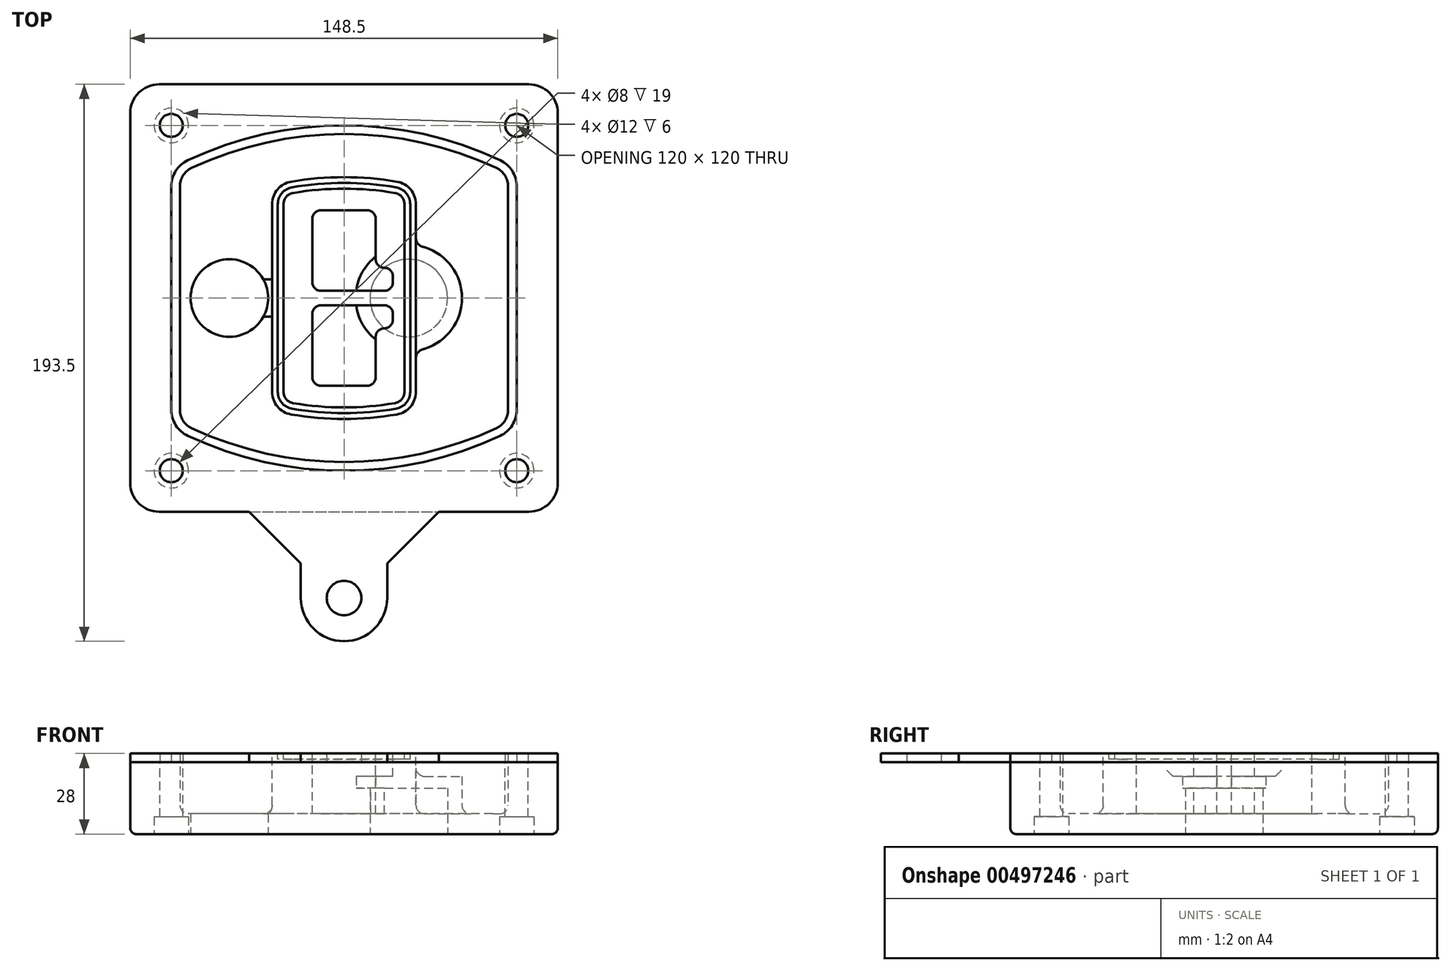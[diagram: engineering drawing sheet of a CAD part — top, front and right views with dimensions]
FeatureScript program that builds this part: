
annotation { "Feature Type Name" : "Feature", "Feature Type Description" : "" }
export const myFeature = defineFeature(function(context is Context, id is Id, definition is map)
    precondition{}
    {
        {
            var Q0;
            Q0=qCreatedBy(makeId("Top.planeOp"),FACE);
            var sketch = newSketch(context, id + "F0", { "sketchPlane" : qUnion([Q0])});
            skPoint(sketch, "E0.rect.middle", {"position": v(0, 0) * mm});
            skLineSegment(sketch, "E1.bottom", {"start": v(-64.25, -74.25) * mm, "end": v(64.25, -74.25) * mm});
            skLineSegment(sketch, "E1.top", {"start": v(-64.25, 74.25) * mm, "end": v(64.25, 74.25) * mm});
            skLineSegment(sketch, "E1.left", {"start": v(-74.25, -64.25) * mm, "end": v(-74.25, 64.25) * mm});
            skLineSegment(sketch, "E1.right", {"start": v(74.25, -64.25) * mm, "end": v(74.25, 64.25) * mm});
            skLineSegment(sketch, "E2", {"start": v(-74.25, 74.25) * mm, "end": v(74.25, -74.25) * mm, "construction": true});
            skLineSegment(sketch, "E3", {"start": v(74.25, 74.25) * mm, "end": v(-74.25, -74.25) * mm, "construction": true});
            skCircle(sketch, "E4", {"center": v(-60, 60) * mm, "radius": 4 * mm});
            skCircle(sketch, "E5", {"center": v(60, 60) * mm, "radius": 4 * mm});
            skCircle(sketch, "E6", {"center": v(60, -60) * mm, "radius": 4 * mm});
            skCircle(sketch, "E7", {"center": v(-60, -60) * mm, "radius": 4 * mm});
            skLineSegment(sketch, "E8", {"start": v(-60, 60) * mm, "end": v(60, 60) * mm, "construction": true});
            skLineSegment(sketch, "E9", {"start": v(60, 60) * mm, "end": v(60, -60) * mm, "construction": true});
            skLineSegment(sketch, "E10", {"start": v(60, -60) * mm, "end": v(-60, -60) * mm, "construction": true});
            skLineSegment(sketch, "E11", {"start": v(-60, -60) * mm, "end": v(-60, 60) * mm, "construction": true});
            skLineSegment(sketch, "E12", {"start": v(-60, 38.83) * mm, "end": v(-60, -38.83) * mm});
            skLineSegment(sketch, "E13", {"start": v(60, 38.83) * mm, "end": v(60, -38.83) * mm});
            skArc(sketch, "E14", {"start": v(54.26, 47.88) * mm, "mid": v(0, 60) * mm, "end": v(-54.26, 47.88) * mm});
            skArc(sketch, "E15", {"start": v(-54.26, -47.88) * mm, "mid": v(0, -60) * mm, "end": v(54.26, -47.88) * mm});
            skLineSegment(sketch, "E16", {"start": v(-60, 0) * mm, "end": v(60, 0) * mm, "construction": true});
            skPoint(sketch, "E17.visualSharp", {"position": v(-60, -45) * mm});
            skArc(sketch, "E17.filletArc", {"start": v(-60, -38.83) * mm, "mid": v(-58.44, -44.2) * mm, "end": v(-54.26, -47.88) * mm});
            skPoint(sketch, "E18.visualSharp", {"position": v(-60, 45) * mm});
            skArc(sketch, "E18.filletArc", {"start": v(-54.26, 47.88) * mm, "mid": v(-58.44, 44.2) * mm, "end": v(-60, 38.83) * mm});
            skPoint(sketch, "E19.visualSharp", {"position": v(60, 45) * mm});
            skArc(sketch, "E19.filletArc", {"start": v(60, 38.83) * mm, "mid": v(58.44, 44.2) * mm, "end": v(54.26, 47.88) * mm});
            skPoint(sketch, "E20.visualSharp", {"position": v(60, -45) * mm});
            skArc(sketch, "E20.filletArc", {"start": v(54.26, -47.88) * mm, "mid": v(58.44, -44.2) * mm, "end": v(60, -38.83) * mm});
            skPoint(sketch, "E21.visualSharp", {"position": v(-74.25, 74.25) * mm});
            skArc(sketch, "E21.filletArc", {"start": v(-64.25, 74.25) * mm, "mid": v(-71.32, 71.32) * mm, "end": v(-74.25, 64.25) * mm});
            skPoint(sketch, "E22.visualSharp", {"position": v(74.25, 74.25) * mm});
            skArc(sketch, "E22.filletArc", {"start": v(74.25, 64.25) * mm, "mid": v(71.32, 71.32) * mm, "end": v(64.25, 74.25) * mm});
            skPoint(sketch, "E23.visualSharp", {"position": v(74.25, -74.25) * mm});
            skArc(sketch, "E23.filletArc", {"start": v(64.25, -74.25) * mm, "mid": v(71.32, -71.32) * mm, "end": v(74.25, -64.25) * mm});
            skPoint(sketch, "E24.visualSharp", {"position": v(-74.25, -74.25) * mm});
            skArc(sketch, "E24.filletArc", {"start": v(-74.25, -64.25) * mm, "mid": v(-71.32, -71.32) * mm, "end": v(-64.25, -74.25) * mm});
            skArc(sketch, "E25.0", {"start": v(57, 38.83) * mm, "mid": v(55.9, 42.58) * mm, "end": v(52.98, 45.17) * mm});
            skLineSegment(sketch, "E25.1", {"start": v(57, 38.83) * mm, "end": v(57, -38.83) * mm});
            skArc(sketch, "E25.2", {"start": v(52.98, -45.17) * mm, "mid": v(55.9, -42.58) * mm, "end": v(57, -38.83) * mm});
            skArc(sketch, "E25.3", {"start": v(-52.98, -45.17) * mm, "mid": v(0, -57) * mm, "end": v(52.98, -45.17) * mm});
            skArc(sketch, "E25.4", {"start": v(-57, -38.83) * mm, "mid": v(-55.9, -42.58) * mm, "end": v(-52.98, -45.17) * mm});
            skArc(sketch, "E25.5", {"start": v(52.98, 45.17) * mm, "mid": v(0, 57) * mm, "end": v(-52.98, 45.17) * mm});
            skLineSegment(sketch, "E25.6", {"start": v(-57, 38.83) * mm, "end": v(-57, -38.83) * mm});
            skArc(sketch, "E25.7", {"start": v(-52.98, 45.17) * mm, "mid": v(-55.9, 42.58) * mm, "end": v(-57, 38.83) * mm});
            skArc(sketch, "E26.0", {"start": v(-55.96, 51.5) * mm, "mid": v(-61.82, 46.33) * mm, "end": v(-64, 38.83) * mm});
            skArc(sketch, "E26.1", {"start": v(55.96, 51.5) * mm, "mid": v(0, 64) * mm, "end": v(-55.96, 51.5) * mm});
            skArc(sketch, "E26.2", {"start": v(64, 38.83) * mm, "mid": v(61.82, 46.33) * mm, "end": v(55.96, 51.5) * mm});
            skLineSegment(sketch, "E26.3", {"start": v(64, 38.83) * mm, "end": v(64, -38.83) * mm});
            skArc(sketch, "E26.4", {"start": v(55.96, -51.5) * mm, "mid": v(61.82, -46.33) * mm, "end": v(64, -38.83) * mm});
            skLineSegment(sketch, "E26.5", {"start": v(-64, 38.83) * mm, "end": v(-64, -38.83) * mm});
            skArc(sketch, "E26.6", {"start": v(-55.96, -51.5) * mm, "mid": v(0, -64) * mm, "end": v(55.96, -51.5) * mm});
            skArc(sketch, "E26.7", {"start": v(-64, -38.83) * mm, "mid": v(-61.82, -46.33) * mm, "end": v(-55.96, -51.5) * mm});
            skSolve(sketch);
        }
        {
            var Q0;
            Q0=makeQuery(id+"F0.imprint","IMPRINT",FACE,{"disambiguationData":[TD([[makeQuery(id+"F0.imprint","IMPRINT",EDGE,{"derivedFrom":sQuery(id+"F0.wireOp",EDGE,"E1.bottom")}),1.0]])]});
            var Q1;
            Q1=makeQuery(id+"F0.imprint","IMPRINT",FACE,{"disambiguationData":[TD([[makeQuery(id+"F0.imprint","IMPRINT",EDGE,{"derivedFrom":sQuery(id+"F0.wireOp",EDGE,"E12")}),1.0]])]});
            var Q2;
            Q2=makeQuery(id+"F0.imprint","IMPRINT",FACE,{"disambiguationData":[TD([[makeQuery(id+"F0.imprint","IMPRINT",EDGE,{"derivedFrom":sQuery(id+"F0.wireOp",EDGE,"E25.0")}),1.0]])]});
            var Q3;
            Q3=makeQuery(id+"F0.imprint","IMPRINT",FACE,{"disambiguationData":[TD([[makeQuery(id+"F0.imprint","IMPRINT",EDGE,{"derivedFrom":sQuery(id+"F0.wireOp",EDGE,"E12")}),-1.0]])]});
            extrude(context, id + "F1", {"entities" : qUnion([Q0, Q1, Q2, Q3]), "oppositeDirection" : true, "depth" : 25 * mm});
        }
        {
            var Q0;
            Q0=makeQuery(id+"F0.imprint","IMPRINT",FACE,{"disambiguationData":[TD([[makeQuery(id+"F0.imprint","IMPRINT",EDGE,{"derivedFrom":sQuery(id+"F0.wireOp",EDGE,"E12")}),1.0]])]});
            extrude(context, id + "F2", {"entities" : qUnion([Q0]), "operationType" : NewBodyOperationType.ADD, "depth" : 3 * mm});
        }
        {
            var Q0;
            Q0=makeQuery(id+"F0.imprint","IMPRINT",FACE,{"disambiguationData":[TD([[makeQuery(id+"F0.imprint","IMPRINT",EDGE,{"derivedFrom":sQuery(id+"F0.wireOp",EDGE,"E25.0")}),1.0]])]});
            extrude(context, id + "F3", {"entities" : qUnion([Q0]), "operationType" : NewBodyOperationType.REMOVE, "oppositeDirection" : true, "depth" : 18 * mm});
        }
        {
            var Q0;
            Q0=makeQuery(id+"F2.opExtrude","CAP_FACE",FACE,{"disambiguationData":[OSD([sQuery(id+"F0.wireOp",EDGE,"E12"),sQuery(id+"F0.wireOp",EDGE,"E13"),sQuery(id+"F0.wireOp",EDGE,"E14"),sQuery(id+"F0.wireOp",EDGE,"E15"),sQuery(id+"F0.wireOp",EDGE,"E17.filletArc"),sQuery(id+"F0.wireOp",EDGE,"E18.filletArc"),sQuery(id+"F0.wireOp",EDGE,"E19.filletArc"),sQuery(id+"F0.wireOp",EDGE,"E20.filletArc"),sQuery(id+"F0.wireOp",EDGE,"E25.0"),sQuery(id+"F0.wireOp",EDGE,"E25.1"),sQuery(id+"F0.wireOp",EDGE,"E25.2"),sQuery(id+"F0.wireOp",EDGE,"E25.3"),sQuery(id+"F0.wireOp",EDGE,"E25.4"),sQuery(id+"F0.wireOp",EDGE,"E25.5"),sQuery(id+"F0.wireOp",EDGE,"E25.6"),sQuery(id+"F0.wireOp",EDGE,"E25.7")])],"isStart":false});
            var sketch = newSketch(context, id + "F4", { "sketchPlane" : qUnion([Q0])});
            skArc(sketch, "E27.0", {"start": v(-18.34, -40.45) * mm, "mid": v(0, -42) * mm, "end": v(18.34, -40.45) * mm});
            skArc(sketch, "E28.0", {"start": v(18.34, 40.45) * mm, "mid": v(0, 42) * mm, "end": v(-18.34, 40.45) * mm});
            skLineSegment(sketch, "E29", {"start": v(-25, 32.57) * mm, "end": v(-25, -32.57) * mm});
            skLineSegment(sketch, "E30", {"start": v(25, 32.57) * mm, "end": v(25, -32.57) * mm});
            skLineSegment(sketch, "E31", {"start": v(-25, 39.1) * mm, "end": v(25, 39.1) * mm, "construction": true});
            skLineSegment(sketch, "E32", {"start": v(-25, -39.1) * mm, "end": v(25, -39.1) * mm, "construction": true});
            skPoint(sketch, "E33.visualSharp", {"position": v(-25, 39.1) * mm});
            skArc(sketch, "E33.filletArc", {"start": v(-18.34, 40.45) * mm, "mid": v(-23.11, 37.73) * mm, "end": v(-25, 32.57) * mm});
            skPoint(sketch, "E34.visualSharp", {"position": v(25, 39.1) * mm});
            skArc(sketch, "E34.filletArc", {"start": v(25, 32.57) * mm, "mid": v(23.11, 37.73) * mm, "end": v(18.34, 40.45) * mm});
            skPoint(sketch, "E35.visualSharp", {"position": v(25, -39.1) * mm});
            skArc(sketch, "E35.filletArc", {"start": v(18.34, -40.45) * mm, "mid": v(23.11, -37.73) * mm, "end": v(25, -32.57) * mm});
            skPoint(sketch, "E36.visualSharp", {"position": v(-25, -39.1) * mm});
            skArc(sketch, "E36.filletArc", {"start": v(-25, -32.57) * mm, "mid": v(-23.11, -37.73) * mm, "end": v(-18.34, -40.45) * mm});
            skArc(sketch, "E37.0", {"start": v(52.98, 45.17) * mm, "mid": v(0, 57) * mm, "end": v(-52.98, 45.17) * mm});
            skArc(sketch, "E37.1", {"start": v(-52.98, 45.17) * mm, "mid": v(-55.9, 42.58) * mm, "end": v(-57, 38.83) * mm});
            skLineSegment(sketch, "E37.2", {"start": v(-57, 38.83) * mm, "end": v(-57, -38.83) * mm});
            skArc(sketch, "E37.3", {"start": v(-57, -38.83) * mm, "mid": v(-55.9, -42.58) * mm, "end": v(-52.98, -45.17) * mm});
            skArc(sketch, "E37.4", {"start": v(-52.98, -45.17) * mm, "mid": v(0, -57) * mm, "end": v(52.98, -45.17) * mm});
            skArc(sketch, "E37.5", {"start": v(52.98, -45.17) * mm, "mid": v(55.9, -42.58) * mm, "end": v(57, -38.83) * mm});
            skLineSegment(sketch, "E37.6", {"start": v(57, 38.83) * mm, "end": v(57, -38.83) * mm});
            skArc(sketch, "E37.7", {"start": v(57, 38.83) * mm, "mid": v(55.9, 42.58) * mm, "end": v(52.98, 45.17) * mm});
            skLineSegment(sketch, "E38.0", {"start": v(23, 32.57) * mm, "end": v(23, -32.57) * mm});
            skArc(sketch, "E38.1", {"start": v(18, -38.48) * mm, "mid": v(21.58, -36.44) * mm, "end": v(23, -32.57) * mm});
            skArc(sketch, "E38.2", {"start": v(-18, -38.48) * mm, "mid": v(0, -40) * mm, "end": v(18, -38.48) * mm});
            skArc(sketch, "E38.3", {"start": v(-23, -32.57) * mm, "mid": v(-21.58, -36.44) * mm, "end": v(-18, -38.48) * mm});
            skLineSegment(sketch, "E38.4", {"start": v(-23, 32.57) * mm, "end": v(-23, -32.57) * mm});
            skArc(sketch, "E38.5", {"start": v(23, 32.57) * mm, "mid": v(21.58, 36.44) * mm, "end": v(18, 38.48) * mm});
            skArc(sketch, "E38.6", {"start": v(-18, 38.48) * mm, "mid": v(-21.58, 36.44) * mm, "end": v(-23, 32.57) * mm});
            skArc(sketch, "E38.7", {"start": v(18, 38.48) * mm, "mid": v(0, 40) * mm, "end": v(-18, 38.48) * mm});
            skArc(sketch, "E39.0", {"start": v(21, 32.57) * mm, "mid": v(20.06, 35.15) * mm, "end": v(17.67, 36.5) * mm});
            skLineSegment(sketch, "E39.1", {"start": v(21, 32.57) * mm, "end": v(21, -32.57) * mm});
            skArc(sketch, "E39.2", {"start": v(17.67, -36.5) * mm, "mid": v(20.06, -35.15) * mm, "end": v(21, -32.57) * mm});
            skArc(sketch, "E39.3", {"start": v(-17.67, -36.5) * mm, "mid": v(0, -38) * mm, "end": v(17.67, -36.5) * mm});
            skArc(sketch, "E39.4", {"start": v(-21, -32.57) * mm, "mid": v(-20.06, -35.15) * mm, "end": v(-17.67, -36.5) * mm});
            skArc(sketch, "E39.5", {"start": v(17.67, 36.5) * mm, "mid": v(0, 38) * mm, "end": v(-17.67, 36.5) * mm});
            skLineSegment(sketch, "E39.6", {"start": v(-21, 32.57) * mm, "end": v(-21, -32.57) * mm});
            skArc(sketch, "E39.7", {"start": v(-17.67, 36.5) * mm, "mid": v(-20.06, 35.15) * mm, "end": v(-21, 32.57) * mm});
            skLineSegment(sketch, "E40", {"start": v(-25, 0) * mm, "end": v(25, 0) * mm, "construction": true});
            skLineSegment(sketch, "E41", {"start": v(-11, 5.5) * mm, "end": v(-11, 27.5) * mm});
            skLineSegment(sketch, "E42", {"start": v(-8, 30.5) * mm, "end": v(8, 30.5) * mm});
            skLineSegment(sketch, "E43", {"start": v(11, 27.5) * mm, "end": v(11, 13.5) * mm});
            skLineSegment(sketch, "E44", {"start": v(14, 10.5) * mm, "end": v(14, 10.5) * mm});
            skLineSegment(sketch, "E45", {"start": v(17, 7.5) * mm, "end": v(17, 5.5) * mm});
            skLineSegment(sketch, "E46", {"start": v(14, 2.5) * mm, "end": v(-8, 2.5) * mm});
            skPoint(sketch, "E47.visualSharp", {"position": v(-11, 30.5) * mm});
            skArc(sketch, "E47.filletArc", {"start": v(-8, 30.5) * mm, "mid": v(-10.12, 29.62) * mm, "end": v(-11, 27.5) * mm});
            skPoint(sketch, "E48.visualSharp", {"position": v(11, 30.5) * mm});
            skArc(sketch, "E48.filletArc", {"start": v(11, 27.5) * mm, "mid": v(10.12, 29.62) * mm, "end": v(8, 30.5) * mm});
            skPoint(sketch, "E49.visualSharp", {"position": v(11, 10.5) * mm});
            skArc(sketch, "E49.filletArc", {"start": v(11, 13.5) * mm, "mid": v(11.88, 11.38) * mm, "end": v(14, 10.5) * mm});
            skPoint(sketch, "E50.visualSharp", {"position": v(17, 10.5) * mm});
            skArc(sketch, "E50.filletArc", {"start": v(17, 7.5) * mm, "mid": v(16.12, 9.62) * mm, "end": v(14, 10.5) * mm});
            skPoint(sketch, "E51.visualSharp", {"position": v(17, 2.5) * mm});
            skArc(sketch, "E51.filletArc", {"start": v(14, 2.5) * mm, "mid": v(16.12, 3.38) * mm, "end": v(17, 5.5) * mm});
            skPoint(sketch, "E52.visualSharp", {"position": v(-11, 2.5) * mm});
            skArc(sketch, "E52.filletArc", {"start": v(-11, 5.5) * mm, "mid": v(-10.12, 3.38) * mm, "end": v(-8, 2.5) * mm});
            skLineSegment(sketch, "E53.0.MirrorCS", {"start": v(14, -2.5) * mm, "end": v(-8, -2.5) * mm});
            skArc(sketch, "E54.0.MirrorCS", {"start": v(-11, -5.5) * mm, "mid": v(-10.12, -3.38) * mm, "end": v(-8, -2.5) * mm});
            skLineSegment(sketch, "E55.0.MirrorCS", {"start": v(-11, -5.5) * mm, "end": v(-11, -27.5) * mm});
            skArc(sketch, "E56.0.MirrorCS", {"start": v(-8, -30.5) * mm, "mid": v(-10.12, -29.62) * mm, "end": v(-11, -27.5) * mm});
            skLineSegment(sketch, "E57.0.MirrorCS", {"start": v(-8, -30.5) * mm, "end": v(8, -30.5) * mm});
            skArc(sketch, "E58.0.MirrorCS", {"start": v(11, -27.5) * mm, "mid": v(10.12, -29.62) * mm, "end": v(8, -30.5) * mm});
            skLineSegment(sketch, "E59.0.MirrorCS", {"start": v(11, -27.5) * mm, "end": v(11, -13.5) * mm});
            skArc(sketch, "E60.0.MirrorCS", {"start": v(11, -13.5) * mm, "mid": v(11.88, -11.38) * mm, "end": v(14, -10.5) * mm});
            skArc(sketch, "E61.0.MirrorCS", {"start": v(17, -7.5) * mm, "mid": v(16.12, -9.62) * mm, "end": v(14, -10.5) * mm});
            skLineSegment(sketch, "E62.0.MirrorCS", {"start": v(17, -7.5) * mm, "end": v(17, -5.5) * mm});
            skArc(sketch, "E63.0.MirrorCS", {"start": v(14, -2.5) * mm, "mid": v(16.12, -3.38) * mm, "end": v(17, -5.5) * mm});
            skSolve(sketch);
        }
        {
            var Q0;
            Q0=makeQuery(id+"F4.imprint","IMPRINT",FACE,{"disambiguationData":[TD([[makeQuery(id+"F4.imprint","IMPRINT",EDGE,{"derivedFrom":sQuery(id+"F4.wireOp",EDGE,"E27.0")}),1.0]])]});
            var Q1;
            Q1=makeQuery(id+"F4.imprint","IMPRINT",FACE,{"disambiguationData":[TD([[makeQuery(id+"F4.imprint","IMPRINT",EDGE,{"derivedFrom":sQuery(id+"F4.wireOp",EDGE,"E38.0")}),-1.0]])]});
            var Q2;
            Q2=makeQuery(id+"F4.imprint","IMPRINT",FACE,{"disambiguationData":[TD([[makeQuery(id+"F4.imprint","IMPRINT",EDGE,{"derivedFrom":sQuery(id+"F4.wireOp",EDGE,"E39.0")}),1.0]])]});
            extrude(context, id + "F5", {"entities" : qUnion([Q0, Q1, Q2]), "operationType" : NewBodyOperationType.ADD, "endBound" : BoundingType.UP_TO_NEXT, "oppositeDirection" : true, "depth" : 25 * mm});
        }
        {
            var Q0;
            Q0=makeQuery(id+"F4.imprint","IMPRINT",FACE,{"disambiguationData":[TD([[makeQuery(id+"F4.imprint","IMPRINT",EDGE,{"derivedFrom":sQuery(id+"F4.wireOp",EDGE,"E38.0")}),-1.0]])]});
            extrude(context, id + "F6", {"entities" : qUnion([Q0]), "operationType" : NewBodyOperationType.REMOVE, "oppositeDirection" : true, "depth" : 2 * mm});
        }
        {
            var Q0;
            Q0=makeQuery(id+"F1.opExtrude","CAP_FACE",FACE,{"disambiguationData":[OSD([sQuery(id+"F0.wireOp",EDGE,"E1.bottom"),sQuery(id+"F0.wireOp",EDGE,"E1.top"),sQuery(id+"F0.wireOp",EDGE,"E1.left"),sQuery(id+"F0.wireOp",EDGE,"E1.right"),sQuery(id+"F0.wireOp",EDGE,"E4"),sQuery(id+"F0.wireOp",EDGE,"E5"),sQuery(id+"F0.wireOp",EDGE,"E6"),sQuery(id+"F0.wireOp",EDGE,"E7"),sQuery(id+"F0.wireOp",EDGE,"E21.filletArc"),sQuery(id+"F0.wireOp",EDGE,"E22.filletArc"),sQuery(id+"F0.wireOp",EDGE,"E23.filletArc"),sQuery(id+"F0.wireOp",EDGE,"E24.filletArc")])],"isStart":false});
            var sketch = newSketch(context, id + "F7", { "sketchPlane" : qUnion([Q0])});
            skCircle(sketch, "E64", {"center": v(22.5, 0) * mm, "radius": 13.47 * mm});
            skCircle(sketch, "E65", {"center": v(-39.81, 0) * mm, "radius": 13.47 * mm});
            skLineSegment(sketch, "E66", {"start": v(74.25, 0) * mm, "end": v(-74.25, 0) * mm});
            skCircle(sketch, "E67", {"center": v(22.5, 0) * mm, "radius": 18.47 * mm});
            skCircle(sketch, "E68", {"center": v(60, -60) * mm, "radius": 6 * mm});
            skCircle(sketch, "E69", {"center": v(-60, -60) * mm, "radius": 6 * mm});
            skCircle(sketch, "E70", {"center": v(-60, 60) * mm, "radius": 6 * mm});
            skCircle(sketch, "E71", {"center": v(60, 60) * mm, "radius": 6 * mm});
            skSolve(sketch);
        }
        {
            var Q0;
            {var subQ1=sQuery(id+"F7.wireOp",EDGE,"E66");var subQ4=sQuery(id+"F7.wireOp",EDGE,"E64");var subQ6=makeQuery(id+"F7.imprint","INTERSECT",VERTEX,{"disambiguationData":[OD(0.0)],"derivedFrom":[subQ4,subQ1]});Q0=makeQuery(id+"F7.imprint","IMPRINT",FACE,{"disambiguationData":[TD([[makeQuery(id+"F7.imprint","IMPRINT",EDGE,{"disambiguationData":[TD([[subQ6,-1.0]])],"derivedFrom":subQ4}),-1.0]])]});}
            var Q1;
            {var subQ0=sQuery(id+"F7.wireOp",EDGE,"E66");var subQ1=sQuery(id+"F7.wireOp",EDGE,"E64");var subQ3=makeQuery(id+"F7.imprint","INTERSECT",VERTEX,{"disambiguationData":[OD(0.0)],"derivedFrom":[subQ1,subQ0]});Q1=makeQuery(id+"F7.imprint","IMPRINT",FACE,{"disambiguationData":[TD([[makeQuery(id+"F7.imprint","IMPRINT",EDGE,{"disambiguationData":[TD([[subQ3,-1.0]])],"derivedFrom":subQ1}),1.0]])]});}
            var Q2;
            {var subQ0=sQuery(id+"F7.wireOp",EDGE,"E66");var subQ1=sQuery(id+"F7.wireOp",EDGE,"E64");var subQ3=makeQuery(id+"F7.imprint","INTERSECT",VERTEX,{"disambiguationData":[OD(0.0)],"derivedFrom":[subQ1,subQ0]});Q2=makeQuery(id+"F7.imprint","IMPRINT",FACE,{"disambiguationData":[TD([[makeQuery(id+"F7.imprint","IMPRINT",EDGE,{"disambiguationData":[TD([[subQ3,1.0]])],"derivedFrom":subQ1}),1.0]])]});}
            var Q3;
            {var subQ1=sQuery(id+"F7.wireOp",EDGE,"E66");var subQ4=sQuery(id+"F7.wireOp",EDGE,"E64");var subQ6=makeQuery(id+"F7.imprint","INTERSECT",VERTEX,{"disambiguationData":[OD(0.0)],"derivedFrom":[subQ4,subQ1]});Q3=makeQuery(id+"F7.imprint","IMPRINT",FACE,{"disambiguationData":[TD([[makeQuery(id+"F7.imprint","IMPRINT",EDGE,{"disambiguationData":[TD([[subQ6,1.0]])],"derivedFrom":subQ4}),-1.0]])]});}
            extrude(context, id + "F8", {"entities" : qUnion([Q0, Q1, Q2, Q3]), "operationType" : NewBodyOperationType.ADD, "oppositeDirection" : true, "depth" : 20 * mm});
        }
        {
            var Q0;
            {var subQ0=sQuery(id+"F7.wireOp",EDGE,"E66");var subQ1=sQuery(id+"F7.wireOp",EDGE,"E64");var subQ3=makeQuery(id+"F7.imprint","INTERSECT",VERTEX,{"disambiguationData":[OD(0.0)],"derivedFrom":[subQ1,subQ0]});Q0=makeQuery(id+"F7.imprint","IMPRINT",FACE,{"disambiguationData":[TD([[makeQuery(id+"F7.imprint","IMPRINT",EDGE,{"disambiguationData":[TD([[subQ3,-1.0]])],"derivedFrom":subQ1}),1.0]])]});}
            var Q1;
            {var subQ0=sQuery(id+"F7.wireOp",EDGE,"E66");var subQ1=sQuery(id+"F7.wireOp",EDGE,"E64");var subQ3=makeQuery(id+"F7.imprint","INTERSECT",VERTEX,{"disambiguationData":[OD(0.0)],"derivedFrom":[subQ1,subQ0]});Q1=makeQuery(id+"F7.imprint","IMPRINT",FACE,{"disambiguationData":[TD([[makeQuery(id+"F7.imprint","IMPRINT",EDGE,{"disambiguationData":[TD([[subQ3,1.0]])],"derivedFrom":subQ1}),1.0]])]});}
            extrude(context, id + "F9", {"entities" : qUnion([Q0, Q1]), "operationType" : NewBodyOperationType.REMOVE, "oppositeDirection" : true, "depth" : 16 * mm});
        }
        {
            var Q0;
            {var subQ0=sQuery(id+"F7.wireOp",EDGE,"E66");var subQ1=sQuery(id+"F7.wireOp",EDGE,"E65");var subQ3=makeQuery(id+"F7.imprint","INTERSECT",VERTEX,{"disambiguationData":[OD(0.0)],"derivedFrom":[subQ1,subQ0]});Q0=makeQuery(id+"F7.imprint","IMPRINT",FACE,{"disambiguationData":[TD([[makeQuery(id+"F7.imprint","IMPRINT",EDGE,{"disambiguationData":[TD([[subQ3,-1.0]])],"derivedFrom":subQ1}),1.0]])]});}
            var Q1;
            {var subQ0=sQuery(id+"F7.wireOp",EDGE,"E66");var subQ1=sQuery(id+"F7.wireOp",EDGE,"E65");var subQ3=makeQuery(id+"F7.imprint","INTERSECT",VERTEX,{"disambiguationData":[OD(0.0)],"derivedFrom":[subQ1,subQ0]});Q1=makeQuery(id+"F7.imprint","IMPRINT",FACE,{"disambiguationData":[TD([[makeQuery(id+"F7.imprint","IMPRINT",EDGE,{"disambiguationData":[TD([[subQ3,1.0]])],"derivedFrom":subQ1}),1.0]])]});}
            extrude(context, id + "F10", {"entities" : qUnion([Q0, Q1]), "operationType" : NewBodyOperationType.REMOVE, "oppositeDirection" : true, "depth" : 25 * mm});
        }
        {
            var Q0;
            Q0=makeQuery(id+"F7.imprint","IMPRINT",FACE,{"disambiguationData":[TD([[makeQuery(id+"F7.imprint","IMPRINT",EDGE,{"derivedFrom":sQuery(id+"F7.wireOp",EDGE,"E68")}),1.0]])]});
            var Q1;
            Q1=makeQuery(id+"F7.imprint","IMPRINT",FACE,{"disambiguationData":[TD([[makeQuery(id+"F7.imprint","IMPRINT",EDGE,{"derivedFrom":makeQuery(id+"F1.opExtrude","CAP_EDGE",EDGE,{"disambiguationData":[OSD([sQuery(id+"F0.wireOp",EDGE,"E5")])],"isStart":false})}),-1.0]])]});
            var Q2;
            Q2=makeQuery(id+"F7.imprint","IMPRINT",FACE,{"disambiguationData":[TD([[makeQuery(id+"F7.imprint","IMPRINT",EDGE,{"derivedFrom":sQuery(id+"F7.wireOp",EDGE,"E69")}),1.0]])]});
            var Q3;
            Q3=makeQuery(id+"F7.imprint","IMPRINT",FACE,{"disambiguationData":[TD([[makeQuery(id+"F7.imprint","IMPRINT",EDGE,{"derivedFrom":makeQuery(id+"F1.opExtrude","CAP_EDGE",EDGE,{"disambiguationData":[OSD([sQuery(id+"F0.wireOp",EDGE,"E4")])],"isStart":false})}),-1.0]])]});
            var Q4;
            Q4=makeQuery(id+"F7.imprint","IMPRINT",FACE,{"disambiguationData":[TD([[makeQuery(id+"F7.imprint","IMPRINT",EDGE,{"derivedFrom":sQuery(id+"F7.wireOp",EDGE,"E70")}),1.0]])]});
            var Q5;
            Q5=makeQuery(id+"F7.imprint","IMPRINT",FACE,{"disambiguationData":[TD([[makeQuery(id+"F7.imprint","IMPRINT",EDGE,{"derivedFrom":makeQuery(id+"F1.opExtrude","CAP_EDGE",EDGE,{"disambiguationData":[OSD([sQuery(id+"F0.wireOp",EDGE,"E7")])],"isStart":false})}),-1.0]])]});
            var Q6;
            Q6=makeQuery(id+"F7.imprint","IMPRINT",FACE,{"disambiguationData":[TD([[makeQuery(id+"F7.imprint","IMPRINT",EDGE,{"derivedFrom":sQuery(id+"F7.wireOp",EDGE,"E71")}),1.0]])]});
            var Q7;
            Q7=makeQuery(id+"F7.imprint","IMPRINT",FACE,{"disambiguationData":[TD([[makeQuery(id+"F7.imprint","IMPRINT",EDGE,{"derivedFrom":makeQuery(id+"F1.opExtrude","CAP_EDGE",EDGE,{"disambiguationData":[OSD([sQuery(id+"F0.wireOp",EDGE,"E6")])],"isStart":false})}),-1.0]])]});
            extrude(context, id + "F11", {"entities" : qUnion([Q0, Q1, Q2, Q3, Q4, Q5, Q6, Q7]), "operationType" : NewBodyOperationType.REMOVE, "oppositeDirection" : true, "depth" : 6 * mm});
        }
        {
            var Q0;
            Q0=makeQuery(id+"F9.boolean.opBoolean","COPY",FACE,{"derivedFrom":makeQuery(id+"F9.opExtrude","CAP_FACE",FACE,{"disambiguationData":[OSD([sQuery(id+"F7.wireOp",EDGE,"E64")])],"isStart":false})});
            var sketch = newSketch(context, id + "F12", { "sketchPlane" : qUnion([Q0])});
            skArc(sketch, "E72.0", {"start": v(11, 14.45) * mm, "mid": v(6.45, 9.13) * mm, "end": v(4.2, 2.5) * mm});
            skArc(sketch, "E72.1", {"start": v(4.2, -2.5) * mm, "mid": v(6.45, -9.13) * mm, "end": v(11, -14.45) * mm});
            skLineSegment(sketch, "E73", {"start": v(4.2, -2.5) * mm, "end": v(14, -2.5) * mm});
            skLineSegment(sketch, "E74.0", {"start": v(14, 2.5) * mm, "end": v(4.2, 2.5) * mm});
            skArc(sketch, "E74.1", {"start": v(14, 2.5) * mm, "mid": v(16.12, 3.38) * mm, "end": v(17, 5.5) * mm});
            skLineSegment(sketch, "E74.2", {"start": v(17, 7.5) * mm, "end": v(17, 5.5) * mm});
            skArc(sketch, "E74.3", {"start": v(17, 7.5) * mm, "mid": v(16.12, 9.62) * mm, "end": v(14, 10.5) * mm});
            skArc(sketch, "E74.4", {"start": v(11, 13.5) * mm, "mid": v(11.88, 11.38) * mm, "end": v(14, 10.5) * mm});
            skLineSegment(sketch, "E74.5", {"start": v(11, 14.45) * mm, "end": v(11, 13.5) * mm});
            skLineSegment(sketch, "E74.7", {"start": v(14, -2.5) * mm, "end": v(4.2, -2.5) * mm});
            skArc(sketch, "E74.8", {"start": v(14, -2.5) * mm, "mid": v(16.12, -3.38) * mm, "end": v(17, -5.5) * mm});
            skLineSegment(sketch, "E74.9", {"start": v(17, -7.5) * mm, "end": v(17, -5.5) * mm});
            skArc(sketch, "E74.10", {"start": v(17, -7.5) * mm, "mid": v(16.12, -9.62) * mm, "end": v(14, -10.5) * mm});
            skArc(sketch, "E74.11", {"start": v(11, -13.5) * mm, "mid": v(11.88, -11.38) * mm, "end": v(14, -10.5) * mm});
            skLineSegment(sketch, "E74.12", {"start": v(11, -14.45) * mm, "end": v(11, -13.5) * mm});
            skPoint(sketch, "E75.orphan", {"position": v(11, -27.5) * mm});
            skPoint(sketch, "E76.orphan", {"position": v(-8, -2.5) * mm});
            skPoint(sketch, "E77.orphan", {"position": v(-8, 2.5) * mm});
            skPoint(sketch, "E78.orphan", {"position": v(11, 27.5) * mm});
            skSolve(sketch);
        }
        {
            var Q0;
            {var subQ7=sQuery(id+"F12.wireOp",EDGE,"E72.0");var subQ14=sQuery(id+"F12.wireOp",EDGE,"E72.1");var subQ16=sQuery(id+"F12.wireOp",EDGE,"E74.1");var subQ18=sQuery(id+"F12.wireOp",EDGE,"E74.8");Q0=qUnion([makeQuery(id+"F12.imprint","IMPRINT",FACE,{"disambiguationData":[TD([[makeQuery(id+"F12.imprint","IMPRINT",EDGE,{"derivedFrom":subQ7}),1.0]])]}),makeQuery(id+"F12.imprint","IMPRINT",FACE,{"disambiguationData":[TD([[makeQuery(id+"F12.imprint","IMPRINT",EDGE,{"derivedFrom":subQ14}),1.0]])]}),makeQuery(id+"F12.imprint","IMPRINT",FACE,{"disambiguationData":[TD([[makeQuery(id+"F12.imprint","IMPRINT",EDGE,{"derivedFrom":subQ16}),1.0]])]}),makeQuery(id+"F12.imprint","IMPRINT",FACE,{"disambiguationData":[TD([[makeQuery(id+"F12.imprint","IMPRINT",EDGE,{"derivedFrom":subQ18}),-1.0]])]})]);}
            var Q1;
            Q1=makeQuery(id+"F5.boolean.opBoolean","SPLIT",FACE,{"disambiguationData":[TD([makeQuery(id+"F5.opExtrude","SWEPT_FACE",FACE,{"disambiguationData":[OSD([sQuery(id+"F4.wireOp",EDGE,"E41")])]})])],"derivedFrom":makeQuery(id+"F3.boolean.opBoolean","COPY",FACE,{"derivedFrom":makeQuery(id+"F3.opExtrude","CAP_FACE",FACE,{"disambiguationData":[OSD([sQuery(id+"F0.wireOp",EDGE,"E25.0"),sQuery(id+"F0.wireOp",EDGE,"E25.1"),sQuery(id+"F0.wireOp",EDGE,"E25.2"),sQuery(id+"F0.wireOp",EDGE,"E25.3"),sQuery(id+"F0.wireOp",EDGE,"E25.4"),sQuery(id+"F0.wireOp",EDGE,"E25.5"),sQuery(id+"F0.wireOp",EDGE,"E25.6"),sQuery(id+"F0.wireOp",EDGE,"E25.7")])],"isStart":false})})});
            extrude(context, id + "F13", {"entities" : qUnion([Q0]), "operationType" : NewBodyOperationType.REMOVE, "endBound" : BoundingType.UP_TO_SURFACE, "endBoundEntityFace" : qUnion([Q1]), "depth" : 25 * mm});
        }
        {
            var Q0;
            Q0=makeQuery(id+"F3.boolean.opBoolean","COPY",EDGE,{"derivedFrom":makeQuery(id+"F3.opExtrude","CAP_EDGE",EDGE,{"disambiguationData":[OSD([sQuery(id+"F0.wireOp",EDGE,"E25.6")])],"isStart":false})});
            var Q1;
            Q1=makeQuery(id+"F8.boolean.opBoolean","INTERSECT",EDGE,{"derivedFrom":[makeQuery(id+"F5.opExtrude","SWEPT_FACE",FACE,{"disambiguationData":[OSD([sQuery(id+"F4.wireOp",EDGE,"E30")])]}),makeQuery(id+"F8.opExtrude","CAP_FACE",FACE,{"disambiguationData":[OSD([sQuery(id+"F7.wireOp",EDGE,"E67")])],"isStart":false})]});
            var Q2;
            Q2=makeQuery(id+"F8.boolean.opBoolean","INTERSECT",EDGE,{"disambiguationData":[OD(1.0)],"derivedFrom":[makeQuery(id+"F5.opExtrude","SWEPT_FACE",FACE,{"disambiguationData":[OSD([sQuery(id+"F4.wireOp",EDGE,"E30")])]}),makeQuery(id+"F8.opExtrude","SWEPT_FACE",FACE,{"disambiguationData":[OSD([sQuery(id+"F7.wireOp",EDGE,"E67")])]})]});
            var Q3;
            {var subQ0=sQuery(id+"F4.wireOp",EDGE,"E30");Q3=makeQuery(id+"F8.boolean.opBoolean","SPLIT",EDGE,{"disambiguationData":[TD([makeQuery(id+"F5.opExtrude","SWEPT_FACE",FACE,{"disambiguationData":[OSD([sQuery(id+"F4.wireOp",EDGE,"E35.filletArc")])]})])],"derivedFrom":makeQuery(id+"F5.opExtrude","CAP_EDGE",EDGE,{"disambiguationData":[OSD([subQ0])],"isStart":false})});}
            var Q4;
            {var subQ0=sQuery(id+"F0.wireOp",EDGE,"E25.7");var subQ1=sQuery(id+"F0.wireOp",EDGE,"E25.1");var subQ2=sQuery(id+"F0.wireOp",EDGE,"E25.6");var subQ3=sQuery(id+"F0.wireOp",EDGE,"E25.5");var subQ4=sQuery(id+"F0.wireOp",EDGE,"E25.4");var subQ5=sQuery(id+"F0.wireOp",EDGE,"E25.0");var subQ6=sQuery(id+"F0.wireOp",EDGE,"E25.2");var subQ7=sQuery(id+"F0.wireOp",EDGE,"E25.3");Q4=makeQuery(id+"F8.boolean.opBoolean","INTERSECT",EDGE,{"derivedFrom":[makeQuery(id+"F5.boolean.opBoolean","SPLIT",FACE,{"disambiguationData":[TD([makeQuery(id+"F2.opExtrude","SWEPT_FACE",FACE,{"disambiguationData":[OSD([subQ5])]})])],"derivedFrom":makeQuery(id+"F3.boolean.opBoolean","COPY",FACE,{"derivedFrom":makeQuery(id+"F3.opExtrude","CAP_FACE",FACE,{"disambiguationData":[OSD([subQ5,subQ1,subQ6,subQ7,subQ4,subQ3,subQ2,subQ0])],"isStart":false})})}),makeQuery(id+"F8.opExtrude","SWEPT_FACE",FACE,{"disambiguationData":[OSD([sQuery(id+"F7.wireOp",EDGE,"E67")])]})]});}
            var Q5;
            Q5=makeQuery(id+"F8.boolean.opBoolean","INTERSECT",EDGE,{"disambiguationData":[OD(0.0)],"derivedFrom":[makeQuery(id+"F5.opExtrude","SWEPT_FACE",FACE,{"disambiguationData":[OSD([sQuery(id+"F4.wireOp",EDGE,"E30")])]}),makeQuery(id+"F8.opExtrude","SWEPT_FACE",FACE,{"disambiguationData":[OSD([sQuery(id+"F7.wireOp",EDGE,"E67")])]})]});
            fillet(context, id + "F14", {"entities" : qUnion([Q0, Q1, Q2, Q3, Q4, Q5]), "radius" : 3 * mm, "tangentPropagation" : true, "allowEdgeOverflow" : false});
        }
        {
            var Q0;
            Q0=makeQuery(id+"F1.opExtrude","CAP_EDGE",EDGE,{"disambiguationData":[OSD([sQuery(id+"F0.wireOp",EDGE,"E1.bottom")])],"isStart":false});
            fillet(context, id + "F15", {"entities" : qUnion([Q0]), "radius" : 2 * mm, "tangentPropagation" : true, "allowEdgeOverflow" : false});
        }
        {
            var Q0;
            {var subQ0=sQuery(id+"F0.wireOp",EDGE,"E21.filletArc");var subQ1=sQuery(id+"F0.wireOp",EDGE,"E7");var subQ2=sQuery(id+"F0.wireOp",EDGE,"E6");var subQ3=sQuery(id+"F0.wireOp",EDGE,"E5");var subQ4=sQuery(id+"F0.wireOp",EDGE,"E4");var subQ5=sQuery(id+"F0.wireOp",EDGE,"E22.filletArc");var subQ6=sQuery(id+"F0.wireOp",EDGE,"E1.bottom");var subQ7=sQuery(id+"F0.wireOp",EDGE,"E1.right");var subQ8=sQuery(id+"F0.wireOp",EDGE,"E1.top");var subQ9=sQuery(id+"F0.wireOp",EDGE,"E1.left");var subQ10=sQuery(id+"F0.wireOp",EDGE,"E23.filletArc");var subQ11=sQuery(id+"F0.wireOp",EDGE,"E24.filletArc");Q0=makeQuery(id+"F2.boolean.opBoolean","SPLIT",FACE,{"disambiguationData":[TD([makeQuery(id+"F1.opExtrude","SWEPT_FACE",FACE,{"disambiguationData":[OSD([subQ6])]})])],"derivedFrom":makeQuery(id+"F1.opExtrude","CAP_FACE",FACE,{"disambiguationData":[OSD([subQ6,subQ8,subQ9,subQ7,subQ4,subQ3,subQ2,subQ1,subQ0,subQ5,subQ10,subQ11])],"isStart":true})});}
            var sketch = newSketch(context, id + "F16", { "sketchPlane" : qUnion([Q0])});
            skLineSegment(sketch, "E79", {"start": v(0, 74.25) * mm, "end": v(0, 104.25) * mm, "construction": true});
            skCircle(sketch, "E80", {"center": v(0, 104.25) * mm, "radius": 6 * mm});
            skLineSegment(sketch, "E81", {"start": v(-33, 74.25) * mm, "end": v(-15, 92.25) * mm});
            skLineSegment(sketch, "E82", {"start": v(-15, 92.25) * mm, "end": v(-15, 104.25) * mm});
            skLineSegment(sketch, "E83", {"start": v(33, 74.25) * mm, "end": v(15, 92.25) * mm});
            skLineSegment(sketch, "E84", {"start": v(15, 92.25) * mm, "end": v(15, 104.25) * mm});
            skArc(sketch, "E85", {"start": v(15, 104.25) * mm, "mid": v(0, 119.25) * mm, "end": v(-15, 104.25) * mm});
            skLineSegment(sketch, "E86", {"start": v(-74.25, 0) * mm, "end": v(74.25, 0) * mm, "construction": true});
            skArc(sketch, "E87.MirrorCS", {"start": v(-15, 104.25) * mm, "mid": v(0, 119.25) * mm, "end": v(15, 104.25) * mm});
            skLineSegment(sketch, "E88.MirrorCS", {"start": v(74.25, 0) * mm, "end": v(-74.25, 0) * mm, "construction": true});
            skArc(sketch, "E89.MirrorCS", {"start": v(-15, -104.25) * mm, "mid": v(0, -119.25) * mm, "end": v(15, -104.25) * mm});
            skArc(sketch, "E90.MirrorCS", {"start": v(15, -104.25) * mm, "mid": v(0, -119.25) * mm, "end": v(-15, -104.25) * mm});
            skLineSegment(sketch, "E91.MirrorCS", {"start": v(-33, -74.25) * mm, "end": v(-15, -92.25) * mm});
            skLineSegment(sketch, "E92.MirrorCS", {"start": v(-15, -92.25) * mm, "end": v(-15, -104.25) * mm});
            skCircle(sketch, "E93.MirrorC", {"center": v(0, -104.25) * mm, "radius": 6 * mm});
            skLineSegment(sketch, "E94.MirrorCS", {"start": v(15, -92.25) * mm, "end": v(15, -104.25) * mm});
            skLineSegment(sketch, "E95.MirrorCS", {"start": v(33, -74.25) * mm, "end": v(15, -92.25) * mm});
            skLineSegment(sketch, "E96.MirrorCS", {"start": v(0, -74.25) * mm, "end": v(0, -104.25) * mm, "construction": true});
            skSolve(sketch);
        }
        {
            var Q0;
            Q0=makeQuery(id+"F16.imprint","IMPRINT",FACE,{"disambiguationData":[TD([[makeQuery(id+"F16.imprint","IMPRINT",EDGE,{"derivedFrom":sQuery(id+"F16.wireOp",EDGE,"E87.MirrorCS")}),-1.0]])]});
            var Q1;
            Q1=makeQuery(id+"F16.imprint","IMPRINT",FACE,{"disambiguationData":[TD([[makeQuery(id+"F16.imprint","IMPRINT",EDGE,{"derivedFrom":makeQuery(id+"F1.opExtrude","CAP_EDGE",EDGE,{"disambiguationData":[OSD([sQuery(id+"F0.wireOp",EDGE,"E1.left")])],"isStart":true})}),-1.0]])]});
            var Q2;
            Q2=makeQuery(id+"F16.imprint","IMPRINT",FACE,{"disambiguationData":[TD([[makeQuery(id+"F16.imprint","IMPRINT",EDGE,{"derivedFrom":sQuery(id+"F16.wireOp",EDGE,"E92.MirrorCS")}),1.0]])]});
            var Q3;
            Q3=makeQuery(id+"F2.opExtrude","CAP_FACE",FACE,{"disambiguationData":[OSD([sQuery(id+"F0.wireOp",EDGE,"E12"),sQuery(id+"F0.wireOp",EDGE,"E13"),sQuery(id+"F0.wireOp",EDGE,"E14"),sQuery(id+"F0.wireOp",EDGE,"E15"),sQuery(id+"F0.wireOp",EDGE,"E17.filletArc"),sQuery(id+"F0.wireOp",EDGE,"E18.filletArc"),sQuery(id+"F0.wireOp",EDGE,"E19.filletArc"),sQuery(id+"F0.wireOp",EDGE,"E20.filletArc"),sQuery(id+"F0.wireOp",EDGE,"E25.0"),sQuery(id+"F0.wireOp",EDGE,"E25.1"),sQuery(id+"F0.wireOp",EDGE,"E25.2"),sQuery(id+"F0.wireOp",EDGE,"E25.3"),sQuery(id+"F0.wireOp",EDGE,"E25.4"),sQuery(id+"F0.wireOp",EDGE,"E25.5"),sQuery(id+"F0.wireOp",EDGE,"E25.6"),sQuery(id+"F0.wireOp",EDGE,"E25.7")])],"isStart":false});
            extrude(context, id + "F17", {"entities" : qUnion([Q0, Q1, Q2]), "endBound" : BoundingType.UP_TO_SURFACE, "endBoundEntityFace" : qUnion([Q3]), "depth" : 25 * mm});
        }
    });
